# Revit family: FP_Revit_18_CI122DTB4_Cooktop_90000837B
name_source: partatom
category: Specialty Equipment
revit_build: Autodesk Revit 2018 (Build: 20170223_1515(x64)
units: mm (PartAtom-declared; Revit-internal decimal feet)

## family parameters
Always vertical = Yes
Cut with Voids When Loaded = Yes
OmniClass Number = 23.40.40.14.17.11
OmniClass Title = Cookers, Ovens, Stoves
Part Type = Normal
Room Calculation Point = No
Round Connector Dimension = Use Diameter
Shared = No
Work Plane-Based = No

## types (1)
- FP_Revit_18_CI122DTB4_Cooktop_90000837B
    Cavity - Depth = 490 mm  [stored 1.60761 ft]
    Cavity - Height = 65 mm  [stored 0.213255 ft]
    Cavity - Width = 270 mm  [stored 0.885827 ft]
    Chassis - Depth = 480 mm  [stored 1.5748 ft]
    Chassis - Height = 62 mm  [stored 0.203412 ft]
    Chassis - Width = 260 mm  [stored 0.853018 ft]
    Clearance - Below = 65 mm  [stored 0.213255 ft]
    Clearance - Below Combustible = 70 mm  [stored 0.229659 ft]
    Clearance - Overhead Combustible = 762 mm  [stored 2.5 ft]
    Clearance - Overhead Non-Combustible = 610 mm  [stored 2.00131 ft]
    Clearance - Overhead Rangehood = 650 mm  [stored 2.13255 ft]
    Clearance - Rear of cooktop to nearest Combustible Surface = 8 mm  [stored 0.0262467 ft]
    Clearance - Side of cooktop to nearest Combustible Surface = 16 mm
    Connector Note - Electrical = 208 or 240 V, 14 A or 16 A, 60 Hz,
    Description = 12" Induction Cooktop
    Manufacturer = Fisher & Paykel Appliances
    Material - Body = Fisher & Paykel - Grey
    Material - Cooktop = Fisher & Paykel - Glass, Black
    Material - Graphics = Fisher & Paykel - Graphics Grey
    Material - Trim = Fisher & Paykel - Aluminium, Dark
    Model = CI122DTB4
    Product - Depth = 530 mm  [stored 1.73885 ft]
    Product - Height = 99 mm  [stored 0.324803 ft]
    Product - Width = 299 mm  [stored 0.980971 ft]
    URL = www.fisherpaykel.com
    Visibility - Clearance Required = Yes

note: [stored X ft] marks values corroborated as IEEE doubles in the binary element streams (Revit-internal decimal feet)

## geometry (parser evidence)
native form markers: Sweep x4
no freeform markers — native parametric forms only
